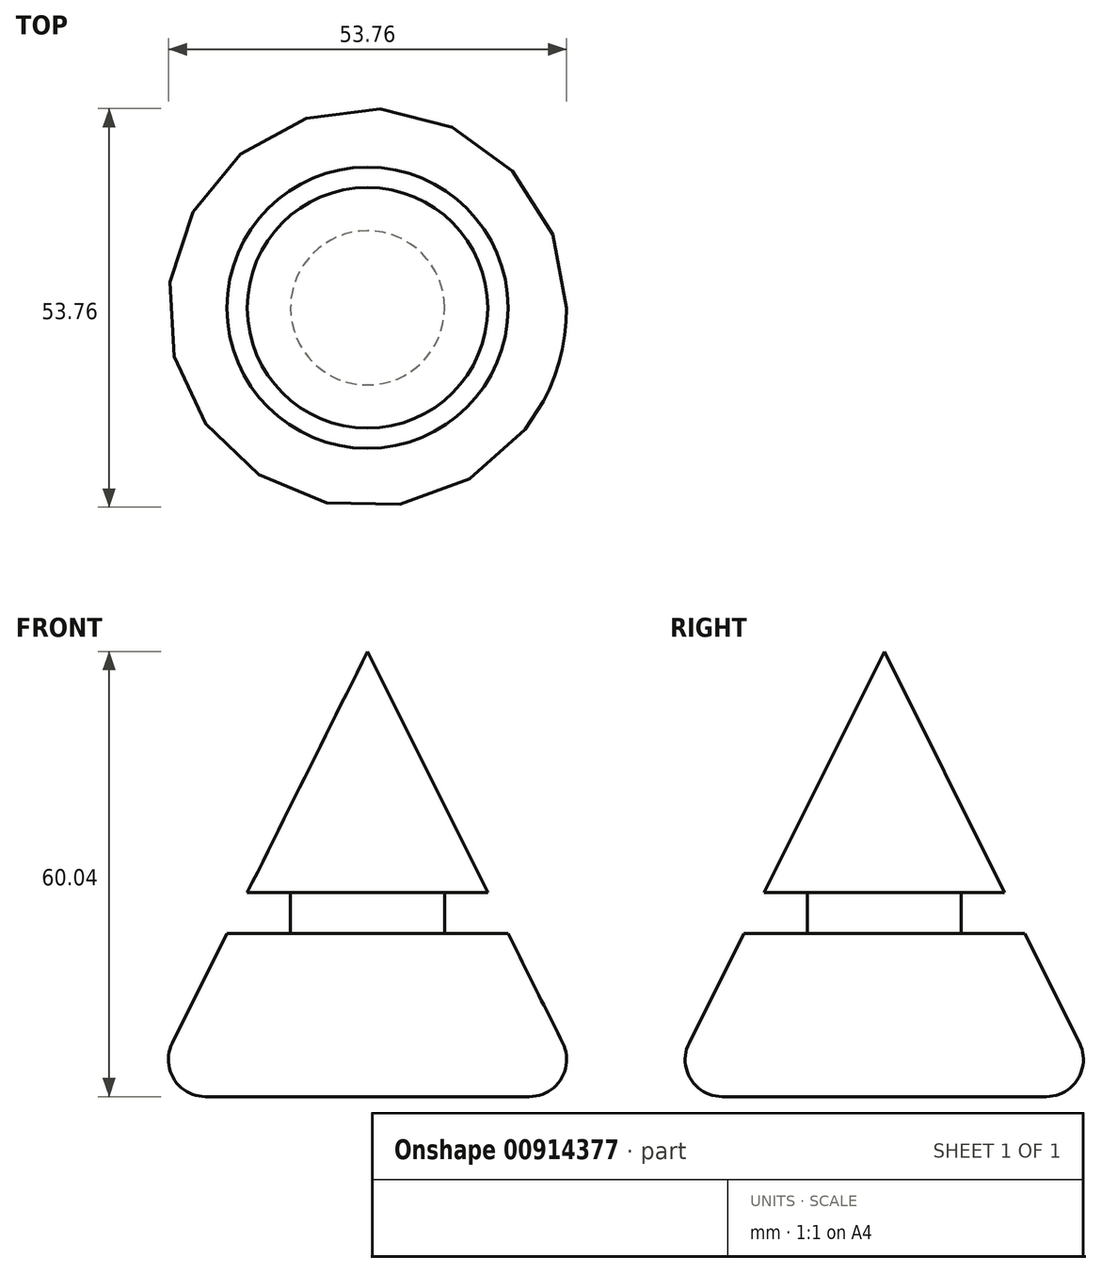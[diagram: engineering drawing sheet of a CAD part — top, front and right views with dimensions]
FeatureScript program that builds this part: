
annotation { "Feature Type Name" : "Feature", "Feature Type Description" : "" }
export const myFeature = defineFeature(function(context is Context, id is Id, definition is map)
    precondition{}
    {
        {
            var Q0;
            Q0=qCreatedBy(makeId("Front.planeOp"),FACE);
            var sketch = newSketch(context, id + "F0", { "sketchPlane" : qUnion([Q0])});
            skLineSegment(sketch, "E0", {"start": v(0, 0) * mm, "end": v(-29.96, 0) * mm});
            skLineSegment(sketch, "E1", {"start": v(-29.96, 0) * mm, "end": v(-18.97, 22.02) * mm});
            skLineSegment(sketch, "E2", {"start": v(0, 60.04) * mm, "end": v(0, 0) * mm});
            skLineSegment(sketch, "E3", {"start": v(-18.97, 22.02) * mm, "end": v(-10.4, 22.02) * mm});
            skLineSegment(sketch, "E4", {"start": v(-10.4, 22.02) * mm, "end": v(-10.4, 27.51) * mm});
            skLineSegment(sketch, "E5", {"start": v(-10.4, 27.51) * mm, "end": v(-16.23, 27.51) * mm});
            skLineSegment(sketch, "E6.trimOffspring", {"start": v(-16.23, 27.51) * mm, "end": v(0, 60.04) * mm});
            skSolve(sketch);
        }
        {
            var Q0;
            Q0=qCreatedBy(makeId("Right.planeOp"),FACE);
            var sketch = newSketch(context, id + "F1", { "sketchPlane" : qUnion([Q0])});
            skLineSegment(sketch, "E7", {"start": v(0, 74.96) * mm, "end": v(0, -27.02) * mm, "construction": true});
            skSolve(sketch);
        }
        {
            var Q0;
            Q0=makeQuery(id+"F0.imprint","IMPRINT",FACE,{"disambiguationData":[TD([[makeQuery(id+"F0.imprint","IMPRINT",EDGE,{"derivedFrom":sQuery(id+"F0.wireOp",EDGE,"E0")}),-1.0]])]});
            var Q1;
            Q1=sQuery(id+"F1.wireOp",EDGE,"E7");
            revolve(context, id + "F2", {"surfaceOperationType" : NewSurfaceOperationType.NEW, "entities" : qUnion([Q0]), "axis" : qUnion([Q1]), "revolveType" : RevolveType.FULL});
        }
        {
            var Q0;
            Q0=makeQuery(id+"F2.opRevolve","SWEPT_EDGE",EDGE,{"disambiguationData":[OSD([sQuery(id+"F0.wireOp",EDGE,"E0"),sQuery(id+"F0.wireOp",EDGE,"E1")])]});
            fillet(context, id + "F3", {"entities" : qUnion([Q0]), "radius" : 5 * mm, "tangentPropagation" : true, "allowEdgeOverflow" : false});
        }
    });
